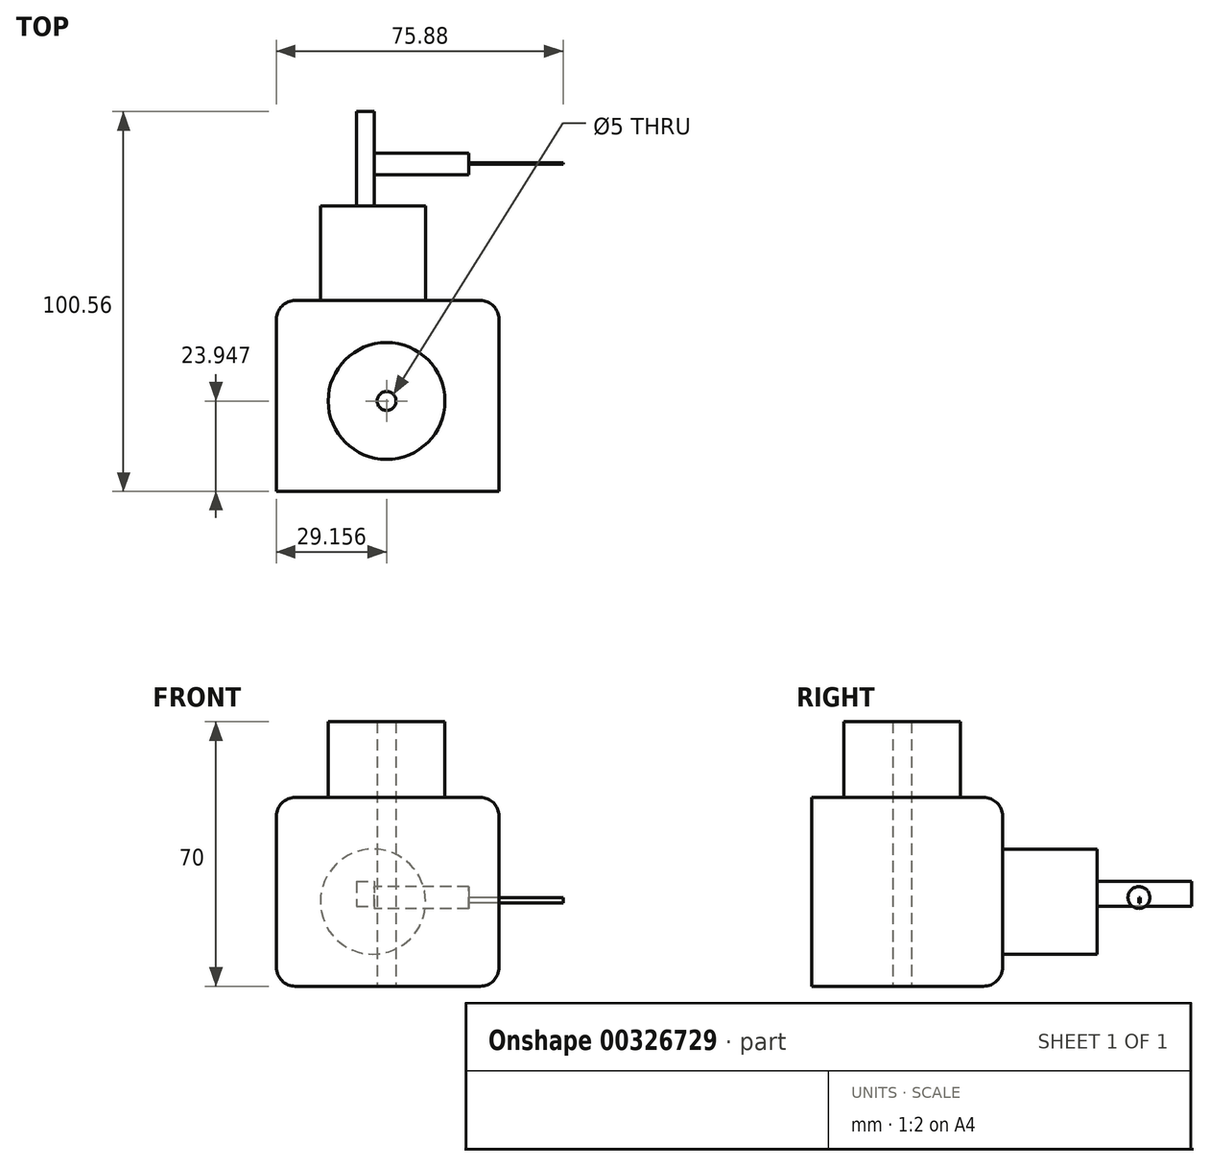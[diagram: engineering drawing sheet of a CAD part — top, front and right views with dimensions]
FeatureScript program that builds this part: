
annotation { "Feature Type Name" : "Feature", "Feature Type Description" : "" }
export const myFeature = defineFeature(function(context is Context, id is Id, definition is map)
    precondition{}
    {
        {
            var Q0;
            Q0=qCreatedBy(makeId("Top.planeOp"),FACE);
            var sketch = newSketch(context, id + "F0", { "sketchPlane" : qUnion([Q0])});
            skLineSegment(sketch, "E0.bottom", {"start": v(0, 0) * mm, "end": v(58.92, 0) * mm});
            skLineSegment(sketch, "E0.top", {"start": v(0, 50.56) * mm, "end": v(58.92, 50.56) * mm});
            skLineSegment(sketch, "E0.left", {"start": v(0, 0) * mm, "end": v(0, 50.56) * mm});
            skLineSegment(sketch, "E0.right", {"start": v(58.92, 0) * mm, "end": v(58.92, 50.56) * mm});
            skSolve(sketch);
        }
        {
            var Q0;
            Q0=makeQuery(id+"F0.imprint","IMPRINT",FACE,{"disambiguationData":[TD([[makeQuery(id+"F0.imprint","IMPRINT",EDGE,{"derivedFrom":sQuery(id+"F0.wireOp",EDGE,"E0.bottom")}),1.0]])]});
            extrude(context, id + "F1", {"entities" : qUnion([Q0]), "oppositeDirection" : true, "depth" : 50 * mm});
        }
        {
            var Q0;
            Q0=makeQuery(id+"F1.opExtrude","SWEPT_FACE",FACE,{"disambiguationData":[OSD([sQuery(id+"F0.wireOp",EDGE,"E0.top")])]});
            var sketch = newSketch(context, id + "F2", { "sketchPlane" : qUnion([Q0])});
            skCircle(sketch, "E1", {"center": v(-25.55, -27.62) * mm, "radius": 13.91 * mm});
            skSolve(sketch);
        }
        {
            var Q0;
            Q0 = qSketchRegion(id + "F2", true);
            extrude(context, id + "F3", {"entities" : qUnion([Q0]), "operationType" : NewBodyOperationType.ADD, "depth" : 25 * mm});
        }
        {
            var Q0;
            Q0=makeQuery(id+"F3.opExtrude","CAP_FACE",FACE,{"disambiguationData":[OSD([sQuery(id+"F2.wireOp",EDGE,"E1")])],"isStart":false});
            var sketch = newSketch(context, id + "F4", { "sketchPlane" : qUnion([Q0])});
            skSolve(sketch);
        }
        {
            var Q0;
            Q0=makeQuery(id+"F4.imprint","IMPRINT",FACE,{"disambiguationData":[TD([[makeQuery(id+"F4.imprint","IMPRINT",EDGE,{"derivedFrom":makeQuery(id+"F3.opExtrude","CAP_EDGE",EDGE,{"disambiguationData":[OSD([sQuery(id+"F2.wireOp",EDGE,"E1")])],"isStart":false})}),1.0]])]});
            var sketch = newSketch(context, id + "F5", { "sketchPlane" : qUnion([Q0])});
            skLineSegment(sketch, "E2.bottom", {"start": v(-21.2, -22.28) * mm, "end": v(-25.88, -22.28) * mm});
            skLineSegment(sketch, "E2.top", {"start": v(-21.2, -28.83) * mm, "end": v(-25.88, -28.83) * mm});
            skLineSegment(sketch, "E2.left", {"start": v(-21.2, -22.28) * mm, "end": v(-21.2, -28.83) * mm});
            skLineSegment(sketch, "E2.right", {"start": v(-25.88, -22.28) * mm, "end": v(-25.88, -28.83) * mm});
            skSolve(sketch);
        }
        {
            var Q0;
            Q0 = qSketchRegion(id + "F5", true);
            extrude(context, id + "F6", {"entities" : qUnion([Q0]), "operationType" : NewBodyOperationType.ADD, "depth" : 25 * mm});
        }
        {
            var Q0;
            Q0=makeQuery(id+"F6.opExtrude","SWEPT_FACE",FACE,{"disambiguationData":[OSD([sQuery(id+"F5.wireOp",EDGE,"E2.right")])]});
            var sketch = newSketch(context, id + "F7", { "sketchPlane" : qUnion([Q0])});
            skCircle(sketch, "E3", {"center": v(86.67, -26.53) * mm, "radius": 2.9 * mm});
            skSolve(sketch);
        }
        {
            var Q0;
            Q0 = qSketchRegion(id + "F7", true);
            extrude(context, id + "F8", {"entities" : qUnion([Q0]), "operationType" : NewBodyOperationType.ADD, "depth" : 25 * mm});
        }
        {
            var Q0;
            Q0=makeQuery(id+"F8.opExtrude","CAP_FACE",FACE,{"disambiguationData":[OSD([sQuery(id+"F7.wireOp",EDGE,"E3")])],"isStart":false});
            var sketch = newSketch(context, id + "F9", { "sketchPlane" : qUnion([Q0])});
            skLineSegment(sketch, "E4.bottom", {"start": v(86.67, -26.53) * mm, "end": v(87, -26.53) * mm});
            skLineSegment(sketch, "E4.top", {"start": v(86.67, -27.97) * mm, "end": v(87, -27.97) * mm});
            skLineSegment(sketch, "E4.left", {"start": v(86.67, -26.53) * mm, "end": v(86.67, -27.97) * mm});
            skLineSegment(sketch, "E4.right", {"start": v(87, -26.53) * mm, "end": v(87, -27.97) * mm});
            skSolve(sketch);
        }
        {
            var Q0;
            Q0 = qSketchRegion(id + "F9", true);
            extrude(context, id + "F10", {"entities" : qUnion([Q0]), "operationType" : NewBodyOperationType.ADD, "depth" : 25 * mm});
        }
        {
            var Q0;
            Q0=makeQuery(id+"F1.opExtrude","CAP_EDGE",EDGE,{"disambiguationData":[OSD([sQuery(id+"F0.wireOp",EDGE,"E0.right")])],"isStart":false});
            fillet(context, id + "F11", {"entities" : qUnion([Q0]), "radius" : 5 * mm, "tangentPropagation" : true, "allowEdgeOverflow" : false});
        }
        {
            var Q0;
            Q0=makeQuery(id+"F1.opExtrude","SWEPT_EDGE",EDGE,{"disambiguationData":[OSD([sQuery(id+"F0.wireOp",EDGE,"E0.top"),sQuery(id+"F0.wireOp",EDGE,"E0.right")])]});
            fillet(context, id + "F12", {"entities" : qUnion([Q0]), "radius" : 5 * mm, "tangentPropagation" : true, "allowEdgeOverflow" : false});
        }
        {
            var Q0;
            Q0=makeQuery(id+"F1.opExtrude","CAP_EDGE",EDGE,{"disambiguationData":[OSD([sQuery(id+"F0.wireOp",EDGE,"E0.left")])],"isStart":false});
            fillet(context, id + "F13", {"entities" : qUnion([Q0]), "radius" : 5 * mm, "tangentPropagation" : true, "allowEdgeOverflow" : false});
        }
        {
            var Q0;
            Q0=makeQuery(id+"F1.opExtrude","CAP_EDGE",EDGE,{"disambiguationData":[OSD([sQuery(id+"F0.wireOp",EDGE,"E0.left")])],"isStart":true});
            fillet(context, id + "F14", {"entities" : qUnion([Q0]), "radius" : 5 * mm, "tangentPropagation" : true, "allowEdgeOverflow" : false});
        }
        {
            var Q0;
            Q0=makeQuery(id+"F1.opExtrude","CAP_FACE",FACE,{"disambiguationData":[OSD([sQuery(id+"F0.wireOp",EDGE,"E0.bottom"),sQuery(id+"F0.wireOp",EDGE,"E0.top"),sQuery(id+"F0.wireOp",EDGE,"E0.left"),sQuery(id+"F0.wireOp",EDGE,"E0.right")])],"isStart":false});
            var sketch = newSketch(context, id + "F15", { "sketchPlane" : qUnion([Q0])});
            skCircle(sketch, "E5", {"center": v(29.16, -23.95) * mm, "radius": 12.1 * mm});
            skSolve(sketch);
        }
        {
            var Q0;
            Q0=sQuery(id+"F15.wireOp",VERTEX,"E5.center");
            var Q1;
            Q1=makeQuery(id+"F1.opExtrude","SWEPT_BODY",BODY,{"disambiguationData":[OSD([sQuery(id+"F0.wireOp",EDGE,"E0.bottom"),sQuery(id+"F0.wireOp",EDGE,"E0.top"),sQuery(id+"F0.wireOp",EDGE,"E0.left"),sQuery(id+"F0.wireOp",EDGE,"E0.right")])]});
            hole(context, id + "F16", {"style" : HoleStyle.SIMPLE, "endStyle" : HoleEndStyle.THROUGH, "holeDiameter" : 5 * mm, "tappedDepth" : 12 * mm, "tapClearance" : 3, "locations" : qUnion([Q0]), "scope" : qUnion([Q1])});
        }
        {
            var Q0;
            Q0=makeQuery(id+"F1.opExtrude","CAP_FACE",FACE,{"disambiguationData":[OSD([sQuery(id+"F0.wireOp",EDGE,"E0.bottom"),sQuery(id+"F0.wireOp",EDGE,"E0.top"),sQuery(id+"F0.wireOp",EDGE,"E0.left"),sQuery(id+"F0.wireOp",EDGE,"E0.right")])],"isStart":true});
            var sketch = newSketch(context, id + "F17", { "sketchPlane" : qUnion([Q0])});
            skCircle(sketch, "E6", {"center": v(29.16, 23.95) * mm, "radius": 17.74 * mm});
            skSolve(sketch);
        }
        {
            var Q0;
            Q0=makeQuery(id+"F17.imprint","IMPRINT",FACE,{"disambiguationData":[TD([[makeQuery(id+"F17.imprint","IMPRINT",EDGE,{"derivedFrom":sQuery(id+"F17.wireOp",EDGE,"E6")}),1.0]])]});
            extrude(context, id + "F18", {"entities" : qUnion([Q0]), "operationType" : NewBodyOperationType.ADD, "oppositeDirection" : true, "depth" : 20 * mm});
        }
        {
            var Q0;
            Q0=makeQuery(id+"F1.opExtrude","CAP_FACE",FACE,{"disambiguationData":[OSD([sQuery(id+"F0.wireOp",EDGE,"E0.bottom"),sQuery(id+"F0.wireOp",EDGE,"E0.top"),sQuery(id+"F0.wireOp",EDGE,"E0.left"),sQuery(id+"F0.wireOp",EDGE,"E0.right")])],"isStart":true});
            var sketch = newSketch(context, id + "F19", { "sketchPlane" : qUnion([Q0])});
            skCircle(sketch, "E7", {"center": v(29.16, 23.95) * mm, "radius": 15.46 * mm});
            skSolve(sketch);
        }
        {
            var Q0;
            Q0=makeQuery(id+"F19.imprint","IMPRINT",FACE,{"disambiguationData":[TD([[makeQuery(id+"F19.imprint","IMPRINT",EDGE,{"derivedFrom":sQuery(id+"F19.wireOp",EDGE,"E7")}),1.0]])]});
            extrude(context, id + "F20", {"entities" : qUnion([Q0]), "operationType" : NewBodyOperationType.ADD, "depth" : 20 * mm});
        }
        {
            var Q0;
            Q0=makeQuery(id+"F1.opExtrude","SWEPT_FACE",FACE,{"disambiguationData":[OSD([sQuery(id+"F0.wireOp",EDGE,"E0.right")])]});
            var sketch = newSketch(context, id + "F21", { "sketchPlane" : qUnion([Q0])});
            skLineSegment(sketch, "E8.bottom", {"start": v(12.65, -34.77) * mm, "end": v(46.02, -34.77) * mm});
            skLineSegment(sketch, "E8.top", {"start": v(12.65, -3.32) * mm, "end": v(46.02, -3.32) * mm});
            skLineSegment(sketch, "E8.left", {"start": v(12.65, -34.77) * mm, "end": v(12.65, -3.32) * mm});
            skLineSegment(sketch, "E8.right", {"start": v(46.02, -34.77) * mm, "end": v(46.02, -3.32) * mm});
            skPoint(sketch, "E8.middle", {"position": v(29.33, -19.05) * mm});
            skSolve(sketch);
        }
        {
            var Q0;
            {var subQ0=sQuery(id+"F21.wireOp",EDGE,"E8.left");var subQ1=sQuery(id+"F21.wireOp",EDGE,"E8.bottom");var subQ2=makeQuery(id+"F21.imprint","INTERSECT",VERTEX,{"derivedFrom":[subQ1,subQ0]});Q0=makeQuery(id+"F21.imprint","IMPRINT",FACE,{"disambiguationData":[TD([[makeQuery(id+"F21.imprint","IMPRINT",EDGE,{"disambiguationData":[TD([[subQ2,-1.0]])],"derivedFrom":subQ0}),-1.0]])]});}
            var Q1;
            Q1 = qSketchRegion(id + "F21", true);
            var Q2;
            Q2=sQuery(id+"F21.wireOp",EDGE,"E8.left");
            extrude(context, id + "F22", {"entities" : qUnion([Q0, Q1]), "bodyType" : ToolBodyType.SURFACE, "surfaceEntities" : qUnion([Q2]), "depth" : 25 * mm});
        }
    });
